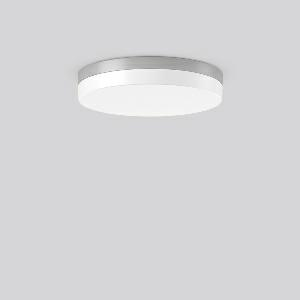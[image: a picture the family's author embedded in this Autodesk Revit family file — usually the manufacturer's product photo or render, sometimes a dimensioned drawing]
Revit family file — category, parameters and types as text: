
# Revit family: flat_slim_round_312632_004_730_4c56
name_source: partatom
category: Lighting Fixtures
units: mm (PartAtom-declared; Revit-internal decimal feet)

## family parameters
Cut with Voids When Loaded = No
Host = Face
Light Source = No
Part Type = Normal
Room Calculation Point = No
Round Connector Dimension = Use Diameter
Shared = No

## types (1)
- MultiLumen 1 830 (1 x LED Modul 830, 2400 lm, 3000)
    Apparent Load = 20 VA
    CIE Flux Codes = 39 70 90 83 100
    Color Rendering = 80
    Color Temperature = 3000
    Default Elevation = 1800 mm
    Height = 70 mm
    Lamp = 1 x LED Modul 830
    Lamp Light Flux = 2400 lm
    Lamp count = 1
    Length = 400 mm
    Lifetime = 50000 h
    Luminous efficacy = 120 lm/W
    Manufacturer = RZB
    ModVariant = No
    Model = 312632.004.730
    Mounting Place = Ceiling
    Mounting Type = Surface mounted
    Number of Poles = 1
    OnlyDefault = Yes
    Power Factor = 1
    Product Name = FLAT SLIM round
    Product group = Surface mounted ceiling and wall luminaires
    ProductGroupID = 305
    Protection Class = Protection class I
    Protection Degree = Degree of protection
    RLX_Detail_Level = 1
    RLX_Emergency_Light_Flux = 0 lm
    RLX_Emergency_Type = 0
    RLX_Emergency_Type_DB = No
    RlxData = <blob elided: 20525 chars, md5=478f9218>
    Socket = socket
    Standby Power = 0 W
    System Light Flux = 2400 lm
    System Power = 20 W
    Type Comments = MultiLumen 1 830
    Type Image = 312631.004.jpg
    URL = http://relux.com
    VarID = multilumen_1_830
    Voltage = 0 V
    Weight = 0.00 kg
    Width = 0 mm  [stored 0 ft]

note: [stored X ft] marks values corroborated as IEEE doubles in the binary element streams (Revit-internal decimal feet)

## geometry (parser evidence)
native form markers: Blend x4, Sweep x13
no freeform markers — native parametric forms only
